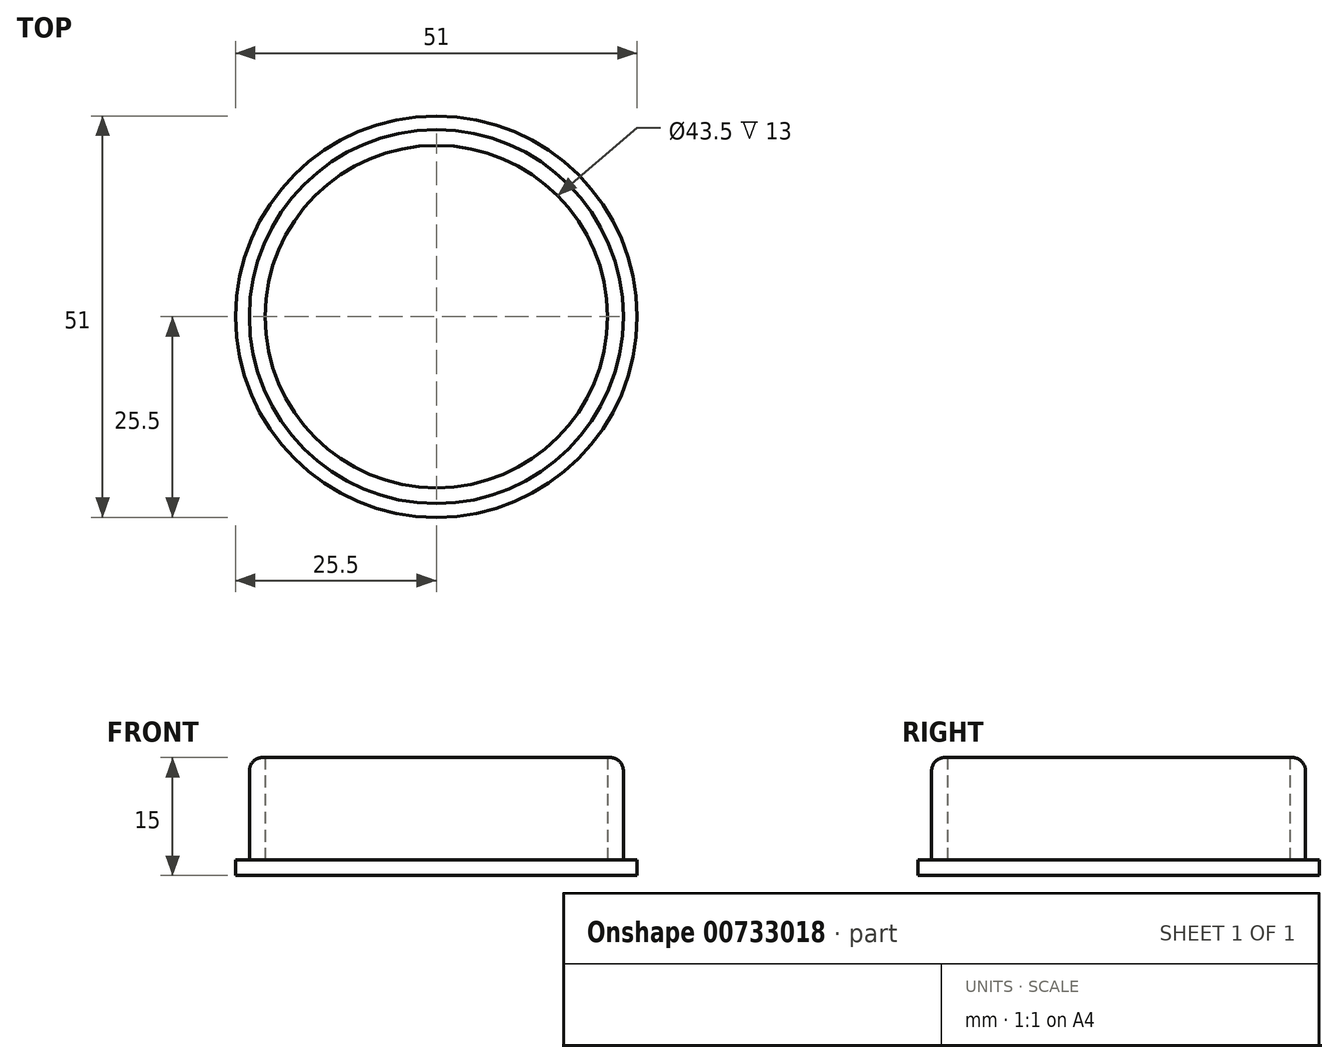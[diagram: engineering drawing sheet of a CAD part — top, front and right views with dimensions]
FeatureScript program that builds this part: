
annotation { "Feature Type Name" : "Feature", "Feature Type Description" : "" }
export const myFeature = defineFeature(function(context is Context, id is Id, definition is map)
    precondition{}
    {
        {
            var Q0;
            Q0=qCreatedBy(makeId("Top.planeOp"),FACE);
            var sketch = newSketch(context, id + "F0", { "sketchPlane" : qUnion([Q0])});
            skCircle(sketch, "E0", {"center": v(0, 0) * mm, "radius": 25.5 * mm});
            skCircle(sketch, "E1", {"center": v(0, 0) * mm, "radius": 23.75 * mm});
            skCircle(sketch, "E2", {"center": v(0, 0) * mm, "radius": 21.75 * mm});
            skSolve(sketch);
        }
        {
            var Q0;
            Q0=makeQuery(id+"F0.imprint","IMPRINT",FACE,{"disambiguationData":[TD([[makeQuery(id+"F0.imprint","IMPRINT",EDGE,{"derivedFrom":sQuery(id+"F0.wireOp",EDGE,"E2")}),1.0]])]});
            var Q1;
            Q1=makeQuery(id+"F0.imprint","IMPRINT",FACE,{"disambiguationData":[TD([[makeQuery(id+"F0.imprint","IMPRINT",EDGE,{"derivedFrom":sQuery(id+"F0.wireOp",EDGE,"E0")}),1.0]])]});
            var Q2;
            Q2=makeQuery(id+"F0.imprint","IMPRINT",FACE,{"disambiguationData":[TD([[makeQuery(id+"F0.imprint","IMPRINT",EDGE,{"derivedFrom":sQuery(id+"F0.wireOp",EDGE,"E1")}),1.0]])]});
            extrude(context, id + "F1", {"entities" : qUnion([Q0, Q1, Q2]), "depth" : 2 * mm, "offsetDistance" : 25 * mm});
        }
        {
            var Q0;
            Q0=makeQuery(id+"F0.imprint","IMPRINT",FACE,{"disambiguationData":[TD([[makeQuery(id+"F0.imprint","IMPRINT",EDGE,{"derivedFrom":sQuery(id+"F0.wireOp",EDGE,"E1")}),1.0]])]});
            extrude(context, id + "F2", {"entities" : qUnion([Q0]), "operationType" : NewBodyOperationType.ADD, "depth" : 15 * mm, "offsetDistance" : 25 * mm});
        }
        {
            var Q0;
            Q0=makeQuery(id+"F2.opExtrude","CAP_EDGE",EDGE,{"disambiguationData":[OSD([sQuery(id+"F0.wireOp",EDGE,"E1")])],"isStart":false});
            fillet(context, id + "F3", {"entities" : qUnion([Q0]), "radius" : 1.7 * mm, "tangentPropagation" : true, "allowEdgeOverflow" : false});
        }
    });
